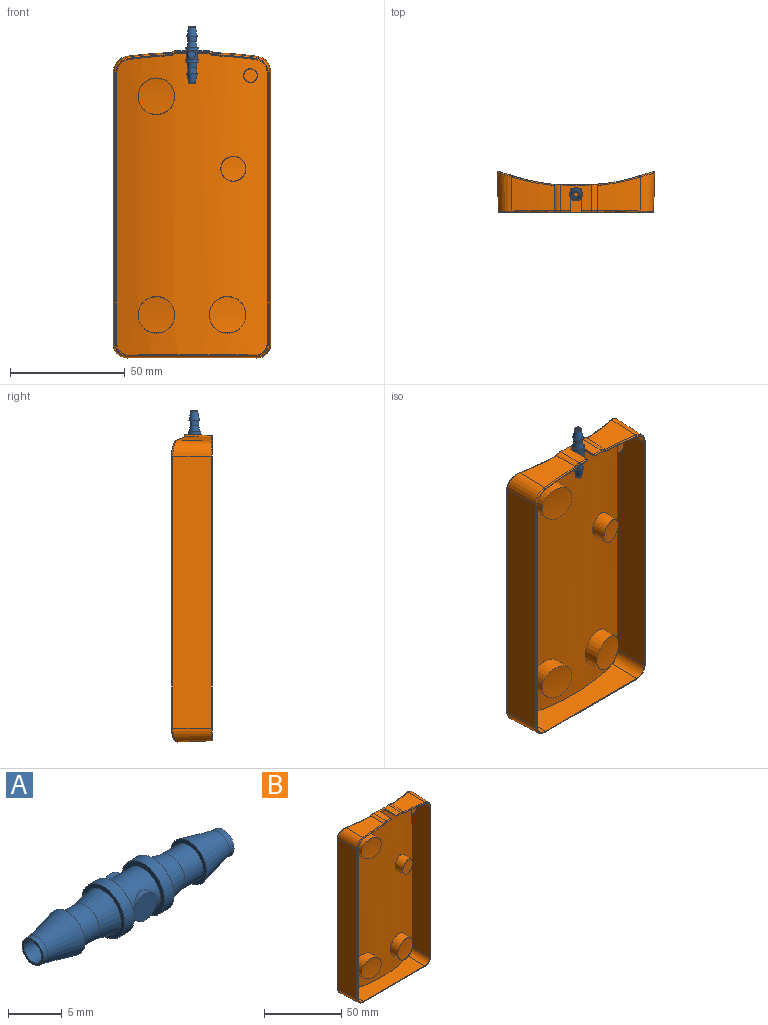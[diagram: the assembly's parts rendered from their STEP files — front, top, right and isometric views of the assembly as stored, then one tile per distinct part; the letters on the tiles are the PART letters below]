
ASSEMBLY  parts=2 mates=1
PART A: 24 faces, bbox 25.1x5.6x5.6 mm
  f0: cylinder r=1.52mm len=3.05mm, axis (0,1,0), area 3mm2, adj f3,f14
  f1: cylinder r=1.52mm len=3.05mm, axis (0,1,0), area 3mm2, adj f3,f13
  f2: cylinder r=1.14mm len=25.07mm, axis (-1,0,0), area 180mm2, adj f11,f22
  f3: cylinder r=2.26mm len=4.51mm, axis (-1,0,0), area 41.2mm2, adj f0,f1,f6,f17
  f4: plane 5.64x5.64mm, normal (1,0,0), area 7.6mm2, adj f7,f12
  f5: cylinder r=1.88mm len=3.76mm, axis (-1,0,0), area 28.1mm2, adj f8,f12
  f6: plane 5.64x5.64mm, normal (-1,0,0), area 9mm2, adj f3,f7
  f7: cylinder r=2.82mm len=5.64mm, axis (-1,0,0), area 22.2mm2, adj f4,f6
  f8: plane 4.7x4.7mm, normal (-1,0,0), area 6.2mm2, adj f5,f9
  f9: cone r=1.43mm half-angle=13.1deg, axis (-1,0,0), area 48.1mm2, adj f8,f10
  f10: cylinder r=1.43mm len=2.86mm, axis (-1,0,0), area 5.1mm2, adj f9,f11
  f11: plane 2.86x2.86mm, normal (1,0,0), area 2.3mm2, adj f2,f10
  f12: cone r=1.88mm half-angle=11.2deg, axis (-1,0,0), area 32.3mm2, adj f4,f5
  f13: plane 3.05x3.05mm, normal (0,1,0), area 7.3mm2, adj f1
  f14: plane 3.05x3.05mm, normal (0,-1,0), area 7.3mm2, adj f0
  f15: plane 5.64x5.64mm, normal (-1,0,0), area 7.6mm2, adj f18,f23
  f16: cylinder r=1.88mm len=3.76mm, axis (1,0,0), area 28.1mm2, adj f19,f23
  f17: plane 5.64x5.64mm, normal (1,0,0), area 9mm2, adj f3,f18
  f18: cylinder r=2.82mm len=5.64mm, axis (1,0,0), area 22.2mm2, adj f15,f17
  f19: plane 4.7x4.7mm, normal (1,0,0), area 6.2mm2, adj f16,f20
  f20: cone r=1.43mm half-angle=13.1deg, axis (1,0,0), area 48.1mm2, adj f19,f21
  f21: cylinder r=1.43mm len=2.86mm, axis (1,0,0), area 5.1mm2, adj f20,f22
  f22: plane 2.86x2.86mm, normal (-1,0,0), area 2.3mm2, adj f2,f21
  f23: cone r=1.88mm half-angle=11.2deg, axis (1,0,0), area 32.3mm2, adj f15,f16
PART B: 72 faces, bbox 77.2x19.7x134.2 mm
  f0: cylinder r=0.5mm len=4.45mm, axis (-1,0,0), area 3.4mm2, adj f3,f15,f25,f70
  f1: cylinder r=96.1mm len=133.45mm, axis (0,0,1), area 8627.6mm2, adj f3,f4,f14,f50,f52,f54,f56,f58
  f2: cylinder r=96.1mm len=131.05mm, axis (0,0,-1), area 7895.6mm2, adj f28,f29,f30,f31,f32,f33,f34,f35
  f3: plane 13.52x11.41mm, normal (0,-0.03,1), area 107.2mm2, adj f0,f1,f4,f14,f23,f69,f70,f71
  f4: cone r=4.17mm half-angle=2deg, axis (0,1,0), area 31.3mm2, adj f1,f3,f5,f25,f60
  f5: cone r=207.86mm half-angle=2deg, axis (0,1,0), area 245.9mm2, adj f4,f6,f27,f60
  f6: cone r=6.5mm half-angle=2deg, axis (0,1,0), area 154.1mm2, adj f5,f7,f26,f61
  f7: plane 118.55x16.77mm, normal (-1,-0.03,0), area 1988.9mm2, adj f6,f8,f24,f62
  f8: cone r=5.5mm half-angle=2deg, axis (0,1,0), area 144mm2, adj f7,f9,f22,f63
  f9: plane 56.5x14.86mm, normal (0,-0.03,-1), area 680.4mm2, adj f8,f10,f20,f64
  f10: cone r=5.5mm half-angle=2deg, axis (0,1,0), area 144mm2, adj f9,f11,f18,f65
  f11: plane 118.55x16.77mm, normal (1,-0.03,0), area 1988.9mm2, adj f10,f12,f16,f66
  f12: cone r=6.5mm half-angle=2deg, axis (0,1,0), area 154.1mm2, adj f11,f13,f17,f67
  f13: cone r=207.86mm half-angle=2deg, axis (0,1,0), area 245.9mm2, adj f12,f14,f19,f68
  f14: cone r=4.17mm half-angle=2deg, axis (0,1,0), area 31.3mm2, adj f1,f3,f13,f21,f68
  f15: plane 132.03x66.53mm, normal (0,-1,0), area 100.9mm2, adj f0,f16,f17,f18,f19,f20,f21,f22
  f16: cylinder r=0.5mm len=118.55mm, axis (0,0,1), area 91mm2, adj f11,f15,f17,f18
  f17: torus R=6.02mm, axis (0,-1,0), area 7mm2, adj f12,f15,f16,f19
  f18: torus R=5.02mm, axis (0,-1,0), area 6.4mm2, adj f10,f15,f16,f20
  f19: torus R=207.38mm, axis (0,-1,0), area 14.6mm2, adj f13,f15,f17,f21
  f20: cylinder r=0.5mm len=56.5mm, axis (1,0,0), area 43.4mm2, adj f9,f15,f18,f22
  f21: torus R=3.68mm, axis (0,-1,0), area 2mm2, adj f14,f15,f19,f23
  f22: torus R=5.02mm, axis (0,-1,0), area 6.4mm2, adj f8,f15,f20,f24
  f23: cylinder r=0.5mm len=4.45mm, axis (-1,0,0), area 3.4mm2, adj f3,f15,f21,f71
  f24: cylinder r=0.5mm len=118.55mm, axis (0,0,-1), area 91mm2, adj f7,f15,f22,f26
  f25: torus R=3.68mm, axis (0,-1,0), area 2mm2, adj f0,f4,f15,f27
  f26: torus R=6.02mm, axis (0,-1,0), area 7mm2, adj f6,f15,f24,f27
  f27: torus R=207.38mm, axis (0,-1,0), area 14.6mm2, adj f5,f15,f25,f26
  f28: cone r=5.75mm half-angle=1deg, axis (0,-1,0), area 125.6mm2, adj f2,f15,f29,f39
  f29: cone r=207.11mm half-angle=1deg, axis (0,-1,0), area 248.3mm2, adj f2,f15,f28,f30
  f30: cone r=3.42mm half-angle=1deg, axis (0,-1,0), area 25.6mm2, adj f2,f15,f29,f31
  f31: plane 13.51x10.89mm, normal (0,-0.02,-1), area 98.1mm2, adj f2,f15,f30,f32,f69,f70,f71
  f32: cone r=3.42mm half-angle=1deg, axis (0,-1,0), area 25.6mm2, adj f2,f15,f31,f33
  f33: cone r=207.11mm half-angle=1deg, axis (0,-1,0), area 248.3mm2, adj f2,f15,f32,f34
  f34: cone r=5.75mm half-angle=1deg, axis (0,-1,0), area 125.6mm2, adj f2,f15,f33,f35
  f35: plane 118.55x16.38mm, normal (1,-0.02,0), area 1942.1mm2, adj f2,f15,f34,f36
  f36: cone r=4.75mm half-angle=1deg, axis (0,-1,0), area 113.3mm2, adj f2,f15,f35,f37
  f37: plane 56.65x15.03mm, normal (0,-0.02,1), area 680.5mm2, adj f2,f15,f36,f38
  f38: cone r=4.75mm half-angle=1deg, axis (0,-1,0), area 113.3mm2, adj f2,f15,f37,f39
  f39: plane 118.55x16.38mm, normal (-1,-0.02,0), area 1942.1mm2, adj f2,f15,f28,f38
  f40: cylinder r=96.14mm len=15.77mm, axis (0,0,-1), area 197.6mm2, adj f41
  f41: cone r=7.5mm half-angle=1deg, axis (0,1,0), area 345mm2, adj f2,f40
  f42: cylinder r=96.14mm len=15.77mm, axis (0,0,-1), area 197.8mm2, adj f43
  f43: cone r=7.5mm half-angle=1deg, axis (0,1,0), area 343.5mm2, adj f2,f42
  f44: cylinder r=96.14mm len=15.77mm, axis (0,0,-1), area 197.8mm2, adj f45
  f45: cone r=7.5mm half-angle=1deg, axis (0,1,0), area 343.5mm2, adj f2,f44
  f46: cylinder r=96.14mm len=10.77mm, axis (0,0,-1), area 92.7mm2, adj f47
  f47: cone r=5mm half-angle=1deg, axis (0,1,0), area 236.7mm2, adj f2,f46
  f48: cylinder r=96.14mm len=5.83mm, axis (0,0,-1), area 27.6mm2, adj f49
  f49: cone r=2.5mm half-angle=1deg, axis (0,1,0), area 129.4mm2, adj f2,f48
  f50: cone r=6.5mm half-angle=1deg, axis (0,1,0), area 280.3mm2, adj f1,f51
  f51: cylinder r=96.14mm len=12.05mm, axis (0,0,-1), area 115.5mm2, adj f50
  f52: cone r=1.5mm half-angle=1deg, axis (0,1,0), area 47.8mm2, adj f1,f53
  f53: cylinder r=96.14mm len=2.12mm, axis (0,0,-1), area 3.6mm2, adj f52
  f54: cone r=4mm half-angle=1deg, axis (0,1,0), area 151.5mm2, adj f1,f55
  f55: cylinder r=96.14mm len=7.06mm, axis (0,0,-1), area 39.8mm2, adj f54
  f56: cone r=6.5mm half-angle=1deg, axis (0,1,0), area 254.4mm2, adj f1,f57
  f57: cylinder r=96.14mm len=12.05mm, axis (0,0,-1), area 115.5mm2, adj f56
  f58: cone r=6.5mm half-angle=1deg, axis (0,1,0), area 280.3mm2, adj f1,f59
  f59: cylinder r=96.14mm len=12.05mm, axis (0,0,-1), area 115.5mm2, adj f58
  f60: bspline ~35.09x8.4mm, area 15.3mm2, adj f1,f4,f5,f61
  f61: bspline ~8.61x7.94mm, area 9.3mm2, adj f1,f6,f60,f62
  f62: cylinder r=0.5mm len=118.55mm, axis (0,0,1), area 116.4mm2, adj f1,f7,f61,f63
  f63: bspline ~7.64x7.41mm, area 8.7mm2, adj f1,f8,f62,f64
  f64: bspline ~56.5x4.72mm, area 45.9mm2, adj f1,f9,f63,f65
  f65: bspline ~7.64x7.41mm, area 8.7mm2, adj f1,f10,f64,f66
  f66: cylinder r=0.5mm len=118.55mm, axis (0,0,1), area 116.4mm2, adj f1,f11,f65,f67
  f67: bspline ~8.61x7.94mm, area 9.3mm2, adj f1,f12,f66,f68
  f68: bspline ~35.09x8.4mm, area 15.3mm2, adj f1,f13,f14,f67
  f69: plane 4.6x1.28mm, normal (0,-1,0.02), area 5.9mm2, adj f3,f31,f70,f71
  f70: plane 10.16x1.28mm, normal (1,0,0), area 10.3mm2, adj f0,f3,f15,f31,f69
  f71: plane 10.16x1.28mm, normal (-1,0,0), area 10.3mm2, adj f3,f15,f23,f31,f69
PLACE A rot(axis=(0.71,0.01,0.71),179.3deg) t=(-2.41,-0.59,71.38)mm
PLACE B rot(axis=(0,-0.02,-1),0deg) t=(-35.16,0.18,-59.23)mm
MATE fastened B.f31 <-> A.f2  axis (0,-0.02,-1) through (-2.41,-0.58,71.88)mm
